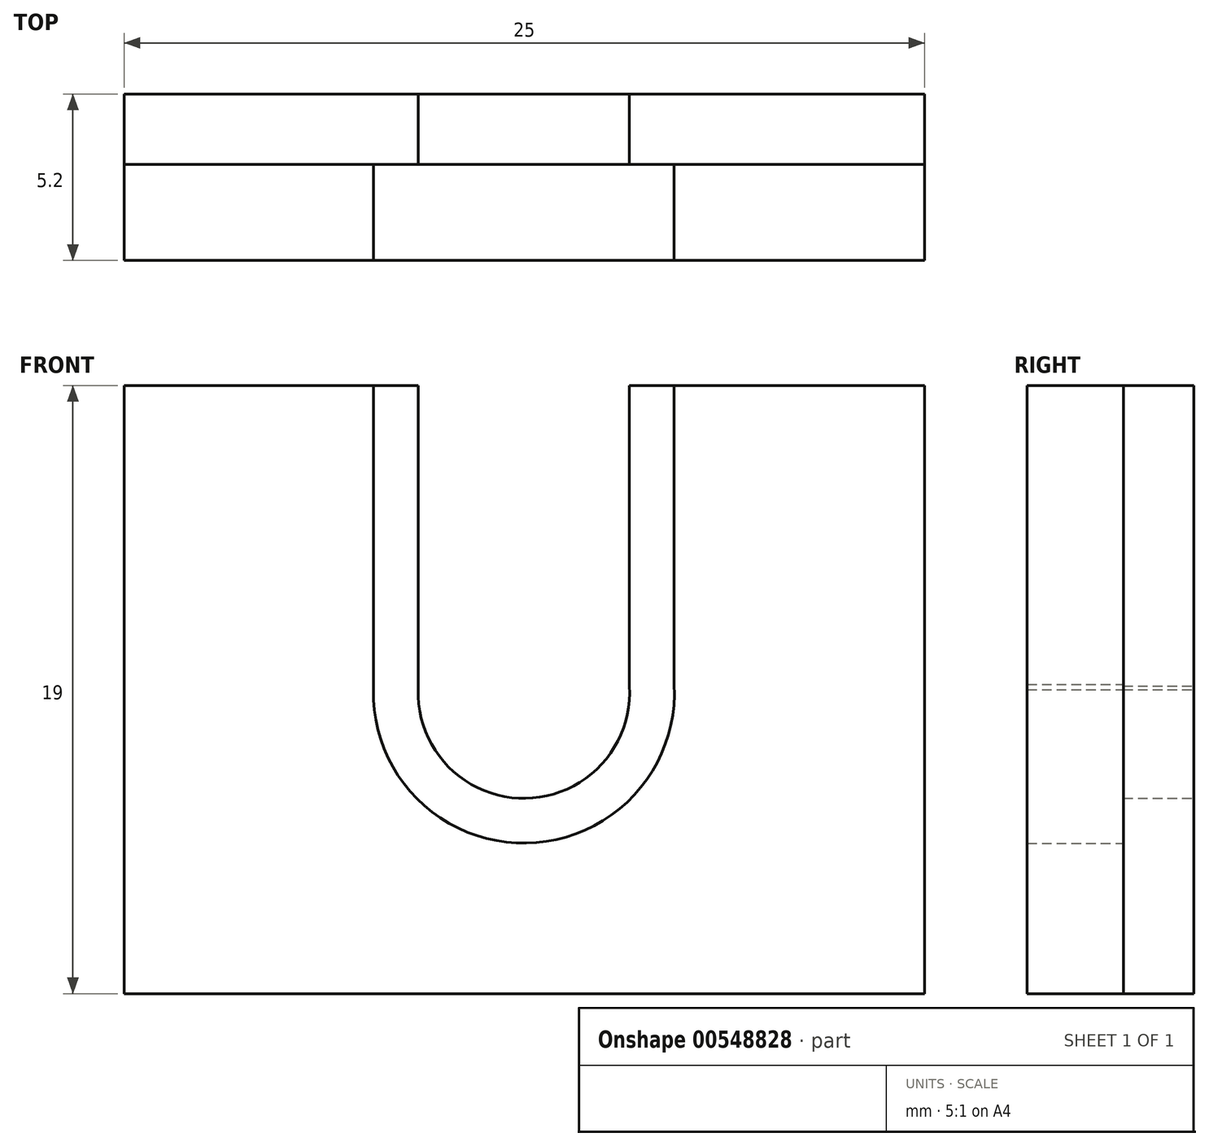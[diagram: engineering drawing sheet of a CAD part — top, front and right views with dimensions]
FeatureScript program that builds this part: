
annotation { "Feature Type Name" : "Feature", "Feature Type Description" : "" }
export const myFeature = defineFeature(function(context is Context, id is Id, definition is map)
    precondition{}
    {
        {
            var Q0;
            Q0=qCreatedBy(makeId("Front.planeOp"),FACE);
            var sketch = newSketch(context, id + "F0", { "sketchPlane" : qUnion([Q0])});
            skLineSegment(sketch, "E0.bottom", {"start": v(12.5, 9.5) * mm, "end": v(3.28, 9.5) * mm});
            skLineSegment(sketch, "E0.top", {"start": v(12.5, -9.5) * mm, "end": v(-12.5, -9.5) * mm});
            skLineSegment(sketch, "E0.left", {"start": v(12.5, 9.5) * mm, "end": v(12.5, -9.5) * mm});
            skLineSegment(sketch, "E0.right", {"start": v(-12.5, 9.5) * mm, "end": v(-12.5, -9.5) * mm});
            skPoint(sketch, "E0.middle", {"position": v(0, 0) * mm});
            skArc(sketch, "E1", {"start": v(-3.31, 0) * mm, "mid": v(0.04, -3.4) * mm, "end": v(3.28, 0.11) * mm});
            skLineSegment(sketch, "E2", {"start": v(3.28, 0.11) * mm, "end": v(3.28, 9.5) * mm});
            skLineSegment(sketch, "E3", {"start": v(-3.31, 0) * mm, "end": v(-3.31, 9.5) * mm});
            skLineSegment(sketch, "E4.trimOffspring", {"start": v(-3.31, 9.5) * mm, "end": v(-12.5, 9.5) * mm});
            skSolve(sketch);
        }
        {
            var Q0;
            Q0 = qSketchRegion(id + "F0", true);
            extrude(context, id + "F1", {"entities" : qUnion([Q0]), "depth" : 2.2 * mm, "offsetDistance" : 25 * mm});
        }
        {
            var Q0;
            Q0=makeQuery(id+"F1.opExtrude","CAP_FACE",FACE,{"disambiguationData":[OSD([sQuery(id+"F0.wireOp",EDGE,"E0.bottom"),sQuery(id+"F0.wireOp",EDGE,"E0.top"),sQuery(id+"F0.wireOp",EDGE,"E0.left"),sQuery(id+"F0.wireOp",EDGE,"E0.right"),sQuery(id+"F0.wireOp",EDGE,"E1"),sQuery(id+"F0.wireOp",EDGE,"E2"),sQuery(id+"F0.wireOp",EDGE,"E3"),sQuery(id+"F0.wireOp",EDGE,"E4.trimOffspring")])],"isStart":false});
            var sketch = newSketch(context, id + "F2", { "sketchPlane" : qUnion([Q0])});
            skLineSegment(sketch, "E5.0.0", {"start": v(-4.72, 0) * mm, "end": v(-4.72, 9.5) * mm});
            skLineSegment(sketch, "E5.0.1", {"start": v(-4.72, 9.5) * mm, "end": v(-12.5, 9.5) * mm});
            skLineSegment(sketch, "E5.0.2", {"start": v(-12.5, 9.5) * mm, "end": v(-12.5, -9.5) * mm});
            skLineSegment(sketch, "E5.0.3", {"start": v(-12.5, -9.5) * mm, "end": v(12.5, -9.5) * mm});
            skLineSegment(sketch, "E5.0.4", {"start": v(12.5, -9.5) * mm, "end": v(12.5, 9.5) * mm});
            skLineSegment(sketch, "E5.0.5", {"start": v(12.5, 9.5) * mm, "end": v(4.68, 9.5) * mm});
            skLineSegment(sketch, "E5.0.6", {"start": v(4.68, 9.5) * mm, "end": v(4.68, 0.11) * mm});
            skArc(sketch, "E5.0.7", {"start": v(3.28, 0.11) * mm, "mid": v(0.04, -3.4) * mm, "end": v(-3.31, 0) * mm});
            skArc(sketch, "E6.0", {"start": v(4.67, 0.2) * mm, "mid": v(0.06, -4.8) * mm, "end": v(-4.71, 0.04) * mm});
            skPoint(sketch, "E7.orphan", {"position": v(3.28, 9.5) * mm});
            skSolve(sketch);
        }
        {
            var Q0;
            Q0 = qSketchRegion(id + "F2", true);
            extrude(context, id + "F3", {"entities" : qUnion([Q0]), "depth" : 3 * mm, "offsetDistance" : 25 * mm});
        }
    });
